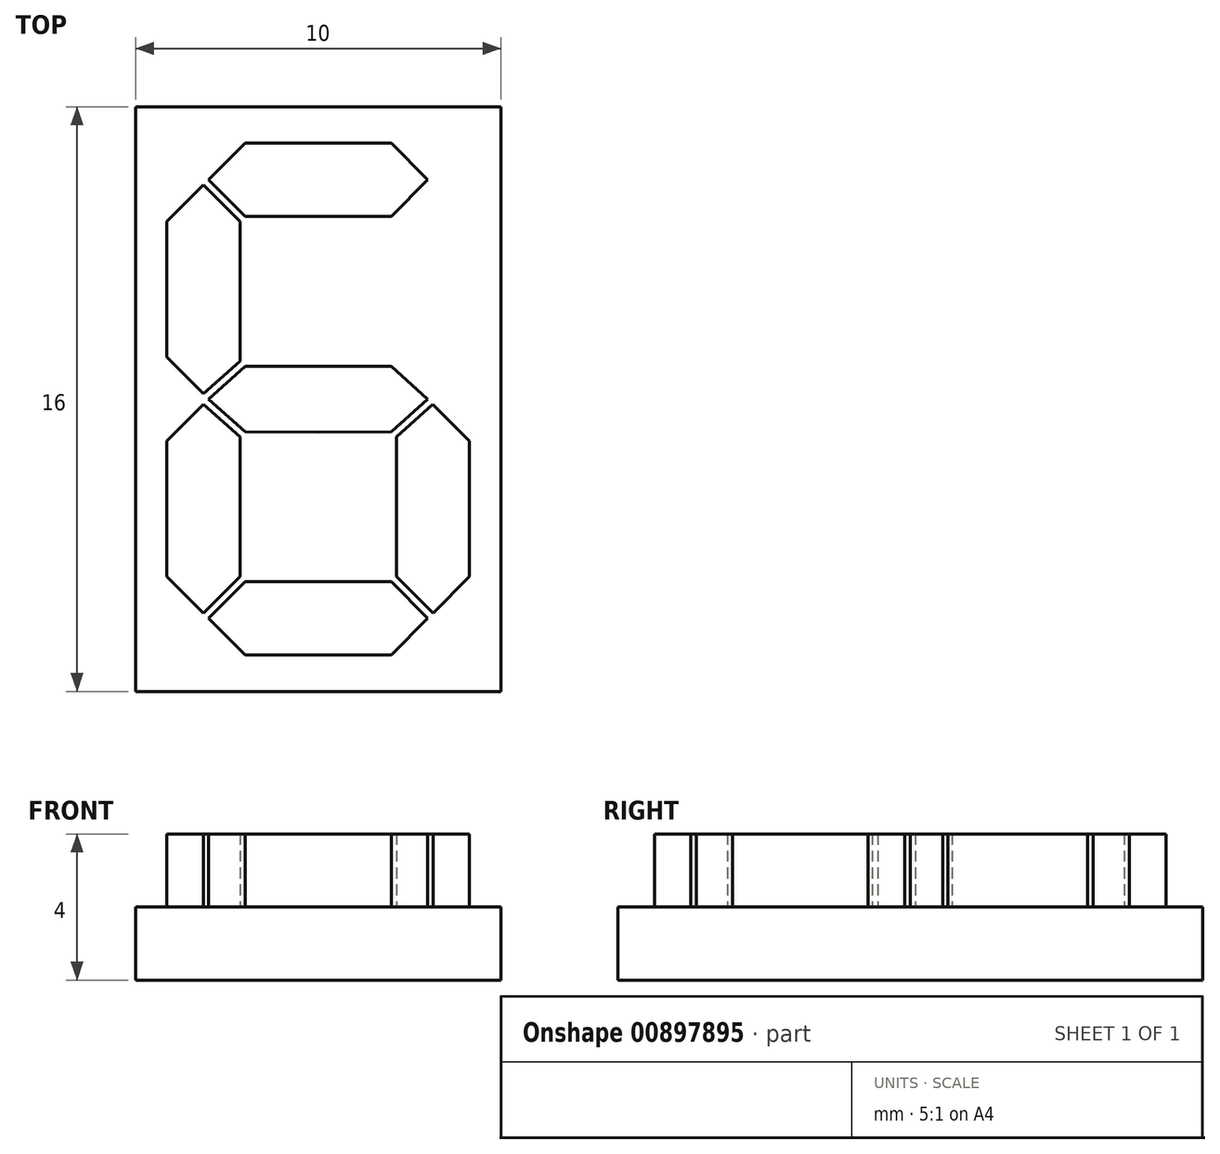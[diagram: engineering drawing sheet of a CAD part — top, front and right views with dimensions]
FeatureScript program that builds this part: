
annotation { "Feature Type Name" : "Feature", "Feature Type Description" : "" }
export const myFeature = defineFeature(function(context is Context, id is Id, definition is map)
    precondition{}
    {
        {
            var Q0;
            Q0=qCreatedBy(makeId("Top.planeOp"),FACE);
            var sketch = newSketch(context, id + "F0", { "sketchPlane" : qUnion([Q0])});
            skLineSegment(sketch, "E0.bottom", {"start": v(5, -8) * mm, "end": v(-5, -8) * mm});
            skLineSegment(sketch, "E0.top", {"start": v(5, 8) * mm, "end": v(-5, 8) * mm});
            skLineSegment(sketch, "E0.left", {"start": v(5, -8) * mm, "end": v(5, 8) * mm});
            skLineSegment(sketch, "E0.right", {"start": v(-5, -8) * mm, "end": v(-5, 8) * mm});
            skPoint(sketch, "E0.middle", {"position": v(0, 0) * mm});
            skSolve(sketch);
        }
        {
            var Q0;
            Q0=makeQuery(id+"F0.imprint","IMPRINT",FACE,{"disambiguationData":[TD([[makeQuery(id+"F0.imprint","IMPRINT",EDGE,{"derivedFrom":sQuery(id+"F0.wireOp",EDGE,"E0.bottom")}),-1.0]])]});
            var Q1;
            Q1 = qSketchRegion(id + "F2", true);
            extrude(context, id + "F1", {"entities" : qUnion([Q0, Q1]), "depth" : 2 * mm, "offsetDistance" : 25 * mm});
        }
        {
            var Q0;
            Q0=makeQuery(id+"F1.opExtrude","CAP_FACE",FACE,{"disambiguationData":[OSD([sQuery(id+"F0.wireOp",EDGE,"E0.bottom"),sQuery(id+"F0.wireOp",EDGE,"E0.top"),sQuery(id+"F0.wireOp",EDGE,"E0.left"),sQuery(id+"F0.wireOp",EDGE,"E0.right")])],"isStart":false});
            var sketch = newSketch(context, id + "F2", { "sketchPlane" : qUnion([Q0])});
            skLineSegment(sketch, "E1", {"start": v(-3, 8) * mm, "end": v(-3, -8) * mm, "construction": true});
            skLineSegment(sketch, "E2.0.1.0", {"start": v(-5, 6) * mm, "end": v(5, 6) * mm, "construction": true});
            skLineSegment(sketch, "E2.direction2", {"start": v(-5, 7) * mm, "end": v(-5, 6) * mm, "construction": true});
            skLineSegment(sketch, "E3.1.0.0", {"start": v(-2, 8) * mm, "end": v(-2, -8) * mm, "construction": true});
            skLineSegment(sketch, "E3.3.0.0", {"start": v(0, 8) * mm, "end": v(0, -8) * mm, "construction": true});
            skLineSegment(sketch, "E3.direction1", {"start": v(-3, -8) * mm, "end": v(-2, -8) * mm, "construction": true});
            skLineSegment(sketch, "E4", {"start": v(-2, 7) * mm, "end": v(-3, 6) * mm});
            skLineSegment(sketch, "E5", {"start": v(-3, 6) * mm, "end": v(-2, 5) * mm});
            skLineSegment(sketch, "E6", {"start": v(-2, 5) * mm, "end": v(0, 5) * mm});
            skLineSegment(sketch, "E7", {"start": v(-2, 7) * mm, "end": v(0, 7) * mm});
            skLineSegment(sketch, "E8.0", {"start": v(-3.14, 5.86) * mm, "end": v(-2.14, 4.86) * mm});
            skLineSegment(sketch, "E9", {"start": v(-2.14, 4.86) * mm, "end": v(-2.14, 1.03) * mm});
            skLineSegment(sketch, "E10.0", {"start": v(-4.14, 4.86) * mm, "end": v(-4.14, 1.15) * mm});
            skLineSegment(sketch, "E11", {"start": v(-3.14, 5.86) * mm, "end": v(-4.14, 4.86) * mm});
            skLineSegment(sketch, "E12", {"start": v(-4.14, 4.86) * mm, "end": v(5, 4.86) * mm, "construction": true});
            skLineSegment(sketch, "E13", {"start": v(0, 0.9) * mm, "end": v(-2, 0.9) * mm});
            skLineSegment(sketch, "E14", {"start": v(-2, 0.9) * mm, "end": v(-3, 0) * mm});
            skLineSegment(sketch, "E15.0", {"start": v(-2.14, 1.03) * mm, "end": v(-3.14, 0.15) * mm});
            skLineSegment(sketch, "E16", {"start": v(-3.14, 5.86) * mm, "end": v(-3.14, 0.15) * mm, "construction": true});
            skLineSegment(sketch, "E17", {"start": v(-4.14, 1.15) * mm, "end": v(-3.14, 0.15) * mm});
            skLineSegment(sketch, "E18.MirrorCS", {"start": v(0, -0.9) * mm, "end": v(-2, -0.9) * mm});
            skLineSegment(sketch, "E19.MirrorCS", {"start": v(-2, -0.9) * mm, "end": v(-3, 0) * mm});
            skLineSegment(sketch, "E20.MirrorCS", {"start": v(-2, -5) * mm, "end": v(0, -5) * mm});
            skLineSegment(sketch, "E21.MirrorCS", {"start": v(-3, -6) * mm, "end": v(-2, -5) * mm});
            skLineSegment(sketch, "E22.MirrorCS", {"start": v(-2, -7) * mm, "end": v(-3, -6) * mm});
            skLineSegment(sketch, "E23.MirrorCS", {"start": v(-2, -7) * mm, "end": v(0, -7) * mm});
            skLineSegment(sketch, "E24.MirrorCS", {"start": v(-3.14, -5.86) * mm, "end": v(-2.14, -4.86) * mm});
            skLineSegment(sketch, "E25.MirrorCS", {"start": v(-3.14, -5.86) * mm, "end": v(-4.14, -4.86) * mm});
            skLineSegment(sketch, "E26.MirrorCS", {"start": v(-4.14, -4.86) * mm, "end": v(-4.14, -1.15) * mm});
            skLineSegment(sketch, "E27.MirrorCS", {"start": v(-4.14, -1.15) * mm, "end": v(-3.14, -0.15) * mm});
            skLineSegment(sketch, "E28.MirrorCS", {"start": v(-2.14, -4.86) * mm, "end": v(-2.14, -1.03) * mm});
            skLineSegment(sketch, "E29.MirrorCS", {"start": v(-2.14, -1.03) * mm, "end": v(-3.14, -0.15) * mm});
            skLineSegment(sketch, "E30.MirrorCS", {"start": v(2, 7) * mm, "end": v(0, 7) * mm});
            skLineSegment(sketch, "E31.MirrorCS", {"start": v(2, 7) * mm, "end": v(3, 6) * mm});
            skLineSegment(sketch, "E32.MirrorCS", {"start": v(3, 6) * mm, "end": v(2, 5) * mm});
            skLineSegment(sketch, "E33.MirrorCS", {"start": v(2, 5) * mm, "end": v(0, 5) * mm});
            skLineSegment(sketch, "E34.MirrorCS", {"start": v(2, 0.9) * mm, "end": v(3, 0) * mm});
            skLineSegment(sketch, "E35.MirrorCS", {"start": v(0, 0.9) * mm, "end": v(2, 0.9) * mm});
            skLineSegment(sketch, "E36.MirrorCS", {"start": v(2, -0.9) * mm, "end": v(3, 0) * mm});
            skLineSegment(sketch, "E37.MirrorCS", {"start": v(0, -0.9) * mm, "end": v(2, -0.9) * mm});
            skLineSegment(sketch, "E38.MirrorCS", {"start": v(2.14, -1.03) * mm, "end": v(3.14, -0.15) * mm});
            skLineSegment(sketch, "E39.MirrorCS", {"start": v(4.14, -1.15) * mm, "end": v(3.14, -0.15) * mm});
            skLineSegment(sketch, "E40.MirrorCS", {"start": v(4.14, -4.86) * mm, "end": v(4.14, -1.15) * mm});
            skLineSegment(sketch, "E41.MirrorCS", {"start": v(2.14, -4.86) * mm, "end": v(2.14, -1.03) * mm});
            skLineSegment(sketch, "E42.MirrorCS", {"start": v(3.14, -5.86) * mm, "end": v(2.14, -4.86) * mm});
            skLineSegment(sketch, "E43.MirrorCS", {"start": v(3.14, -5.86) * mm, "end": v(4.14, -4.86) * mm});
            skLineSegment(sketch, "E44.MirrorCS", {"start": v(3, -6) * mm, "end": v(2, -5) * mm});
            skLineSegment(sketch, "E45.MirrorCS", {"start": v(2, -5) * mm, "end": v(0, -5) * mm});
            skLineSegment(sketch, "E46.MirrorCS", {"start": v(2, -7) * mm, "end": v(3, -6) * mm});
            skLineSegment(sketch, "E47.MirrorCS", {"start": v(2, -7) * mm, "end": v(0, -7) * mm});
            skSolve(sketch);
        }
        {
            var Q0;
            Q0=makeQuery(id+"F2.imprint","IMPRINT",FACE,{"disambiguationData":[TD([[makeQuery(id+"F2.imprint","IMPRINT",EDGE,{"derivedFrom":sQuery(id+"F2.wireOp",EDGE,"E4")}),1.0]])]});
            var Q1;
            Q1=makeQuery(id+"F2.imprint","IMPRINT",FACE,{"disambiguationData":[TD([[makeQuery(id+"F2.imprint","IMPRINT",EDGE,{"derivedFrom":sQuery(id+"F2.wireOp",EDGE,"E8.0")}),-1.0]])]});
            var Q2;
            Q2=makeQuery(id+"F2.imprint","IMPRINT",FACE,{"disambiguationData":[TD([[makeQuery(id+"F2.imprint","IMPRINT",EDGE,{"derivedFrom":sQuery(id+"F2.wireOp",EDGE,"E13")}),1.0]])]});
            var Q3;
            Q3=makeQuery(id+"F2.imprint","IMPRINT",FACE,{"disambiguationData":[TD([[makeQuery(id+"F2.imprint","IMPRINT",EDGE,{"derivedFrom":sQuery(id+"F2.wireOp",EDGE,"E38.MirrorCS")}),-1.0]])]});
            var Q4;
            Q4=makeQuery(id+"F2.imprint","IMPRINT",FACE,{"disambiguationData":[TD([[makeQuery(id+"F2.imprint","IMPRINT",EDGE,{"derivedFrom":sQuery(id+"F2.wireOp",EDGE,"E20.MirrorCS")}),-1.0]])]});
            var Q5;
            Q5=makeQuery(id+"F2.imprint","IMPRINT",FACE,{"disambiguationData":[TD([[makeQuery(id+"F2.imprint","IMPRINT",EDGE,{"derivedFrom":sQuery(id+"F2.wireOp",EDGE,"E24.MirrorCS")}),1.0]])]});
            extrude(context, id + "F3", {"entities" : qUnion([Q0, Q1, Q2, Q3, Q4, Q5]), "operationType" : NewBodyOperationType.ADD, "depth" : 2 * mm, "offsetDistance" : 25 * mm});
        }
    });
